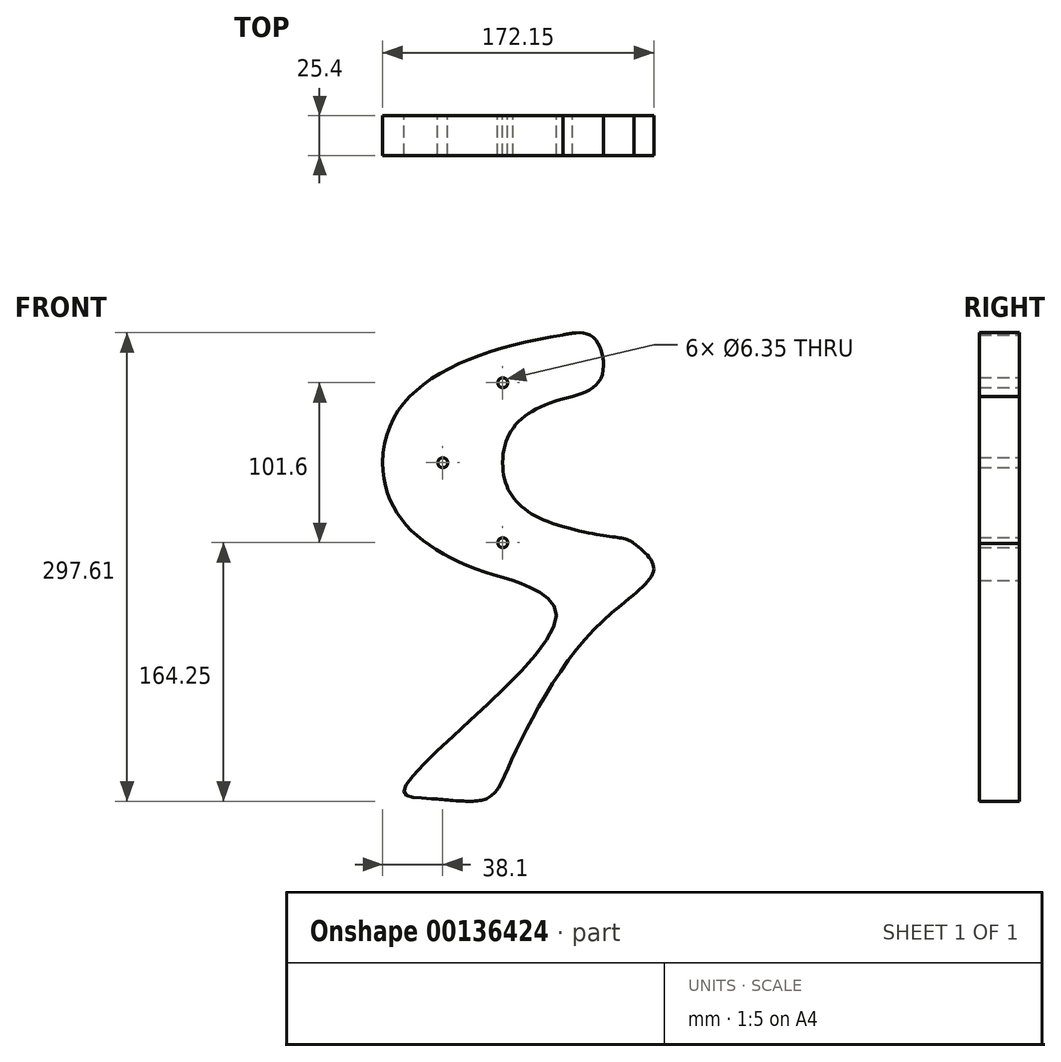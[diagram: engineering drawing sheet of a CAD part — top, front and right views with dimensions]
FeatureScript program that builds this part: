
annotation { "Feature Type Name" : "Feature", "Feature Type Description" : "" }
export const myFeature = defineFeature(function(context is Context, id is Id, definition is map)
    precondition{}
    {
        {
            var Q0;
            Q0=qCreatedBy(makeId("Front.planeOp"),FACE);
            var sketch = newSketch(context, id + "F0", { "sketchPlane" : qUnion([Q0])});
            skLineSegment(sketch, "E0.bottom", {"start": v(228.6, -101.6) * mm, "end": v(-228.6, -101.6) * mm, "construction": true});
            skLineSegment(sketch, "E0.top", {"start": v(228.6, 101.6) * mm, "end": v(-228.6, 101.6) * mm, "construction": true});
            skLineSegment(sketch, "E0.right", {"start": v(-228.6, -101.6) * mm, "end": v(-228.6, 101.6) * mm, "construction": true});
            skLineSegment(sketch, "E1", {"start": v(-228.6, 0) * mm, "end": v(228.6, 0) * mm, "construction": true});
            skLineSegment(sketch, "E2", {"start": v(0, 101.6) * mm, "end": v(0, -101.6) * mm, "construction": true});
            skEllipse(sketch, "E3", {"center": v(0, 0) * mm, "majorRadius": 228.6 * mm, "minorRadius": 101.6 * mm, "majorAxis": v(1, 0), "construction": true});
            skLineSegment(sketch, "E4.0", {"start": v(-228.6, 50.8) * mm, "end": v(228.6, 50.8) * mm, "construction": true});
            skFitSpline(sketch, "E5", {"points": [v(-228.6, 0) * mm, v(0, 50.8) * mm], "startDerivative": vector(0, 152.4) * mm, "endDerivative": vector(467.31, 0) * mm});
            skFitSpline(sketch, "E6.MirrorCS", {"points": [v(-228.6, 0) * mm, v(0, -50.8) * mm], "startDerivative": vector(0, -152.4) * mm, "endDerivative": vector(467.31, 0) * mm});
            skLineSegment(sketch, "E7.0", {"start": v(-304.8, -101.6) * mm, "end": v(-304.8, 101.6) * mm, "construction": true});
            skFitSpline(sketch, "E8", {"points": [v(-304.8, 0) * mm, v(0, 88.9) * mm], "startDerivative": vector(0, 304.8) * mm, "endDerivative": vector(240.47, 1.05) * mm});
            skFitSpline(sketch, "E9.MirrorCS", {"points": [v(-304.8, 0) * mm, v(0, -88.9) * mm], "startDerivative": vector(0, -304.8) * mm, "endDerivative": vector(240.47, -1.05) * mm});
            skLineSegment(sketch, "E10.0", {"start": v(-190.5, 101.6) * mm, "end": v(-190.5, -101.6) * mm, "construction": true});
            skFitSpline(sketch, "E11.MirrorCS", {"points": [v(-190.5, -40.56) * mm, v(-145.73, -50.8) * mm, v(-139.15, -64.98) * mm, v(-153, -82.34) * mm, v(-190.5, -81.2) * mm], "startDerivative": vector(275.6, -78.43) * mm, "endDerivative": vector(-124.93, 13.59) * mm});
            skFitSpline(sketch, "E12", {"points": [v(-222.16, -74.69) * mm, v(-194.6, -98.15) * mm, v(-291.2, -207.38) * mm, v(-273.8, -213.39) * mm, v(-238.83, -213.39) * mm, v(-224.4, -192.11) * mm, v(-169.77, -104.99) * mm, v(-132.65, -67.26) * mm, v(-145.73, -50.8) * mm], "startDerivative": vector(244.93, -116.2) * mm, "endDerivative": vector(-193.53, 147.98) * mm});
            skLineSegment(sketch, "E13", {"start": v(-273.8, -213.39) * mm, "end": v(-238.83, -213.39) * mm});
            skLineSegment(sketch, "E14.0", {"start": v(-266.7, -101.6) * mm, "end": v(-266.7, 101.6) * mm, "construction": true});
            skCircle(sketch, "E15", {"center": v(-228.6, 50.8) * mm, "radius": 3.18 * mm});
            skCircle(sketch, "E16", {"center": v(-266.7, 0) * mm, "radius": 3.18 * mm});
            skCircle(sketch, "E17.MirrorC", {"center": v(-228.6, -50.8) * mm, "radius": 3.18 * mm});
            skLineSegment(sketch, "E18.trimOffspring", {"start": v(-145.73, -50.8) * mm, "end": v(-145.73, -50.8) * mm});
            skLineSegment(sketch, "E19", {"start": v(-145.73, -50.8) * mm, "end": v(-145.23, -51.18) * mm});
            skFitSpline(sketch, "E20", {"points": [v(-190.48, 81.2) * mm, v(-171, 79.56) * mm, v(-166.27, 53.65) * mm, v(-190.48, 40.55) * mm], "startDerivative": vector(72.95, 14.02) * mm, "endDerivative": vector(-86.73, -21.71) * mm});
            skSolve(sketch);
        }
        {
            var Q0;
            Q0=qSketchRegion(id+"F0",true);
            extrude(context, id + "F1", {"entities" : qUnion([Q0]), "depth" : 25.4 * mm});
        }
        {
            var Q0;
            Q0 = qSketchRegion(id + "F0", true);
            extrude(context, id + "F2", {"entities" : qUnion([Q0]), "depth" : 25.4 * mm});
        }
    });
